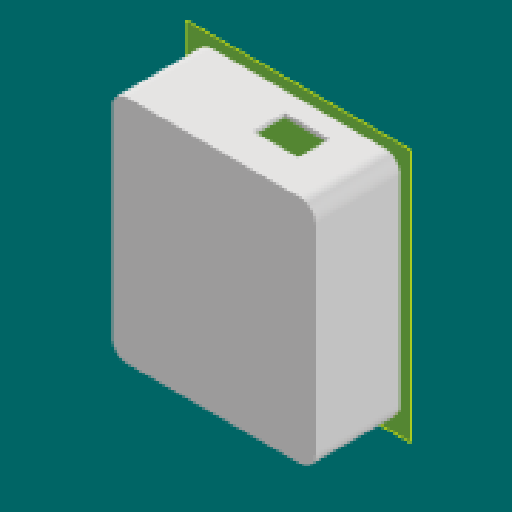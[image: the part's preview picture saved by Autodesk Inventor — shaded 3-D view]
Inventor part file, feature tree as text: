
AUTODESK INVENTOR PART (.ipt)
format: ipt  version: 2025.2 (Build 292293000, 293)  size: 145,408 bytes
history: native  units: mm
features: reference x8, extrude x4, sketch x4, other x4, plane x1
ambient origin geometry x8: Origin, YZ Plane, XZ Plane, XY Plane, X Axis, Y Axis, Z Axis, Center Point
bodies: Solid1 (feature_tree)
feature tree (21):
  plane  "Work Plane1"
  extrude  "Extrusion1"  Depth=2.0mm TaperAngle=0.0deg
  extrude  "Extrusion2"  Depth=0.2mm
  extrude  "Extrusion3"  Depth=16.0mm
  extrude  "Extrusion4"  [1 undecoded]
  sketch  "Sketch1"  dims[d0=27.93mm d1=0.0mm d2=2.0mm d3=0.0mm]
  reference  "Reference1"
  sketch  "Sketch2"  dims[d4=7.45mm d5=0.0mm d6=0.2mm]
  sketch  "Sketch3"  dims[d7=7.45mm d8=0.0mm d9=16.0mm]
  reference  "Reference2"
  reference  "Reference3"
  reference  "Reference4"
  sketch  "Sketch4"
  reference  "Reference5"
  reference  "Reference6"
  reference  "Reference7"
  reference  "Reference8"
  other  "<userpath>\Downloads\cassing_hardware\Assembly1.iam"
  other  "Assembly1.iam"
  other  "part1:1"
  other  "AVR_MasImam:1"
note: 1 required parameter value undecoded (feature->parameter linkage not recoverable at this tier; creation-order binding heuristic only, values carry confidence <= 0.55)
